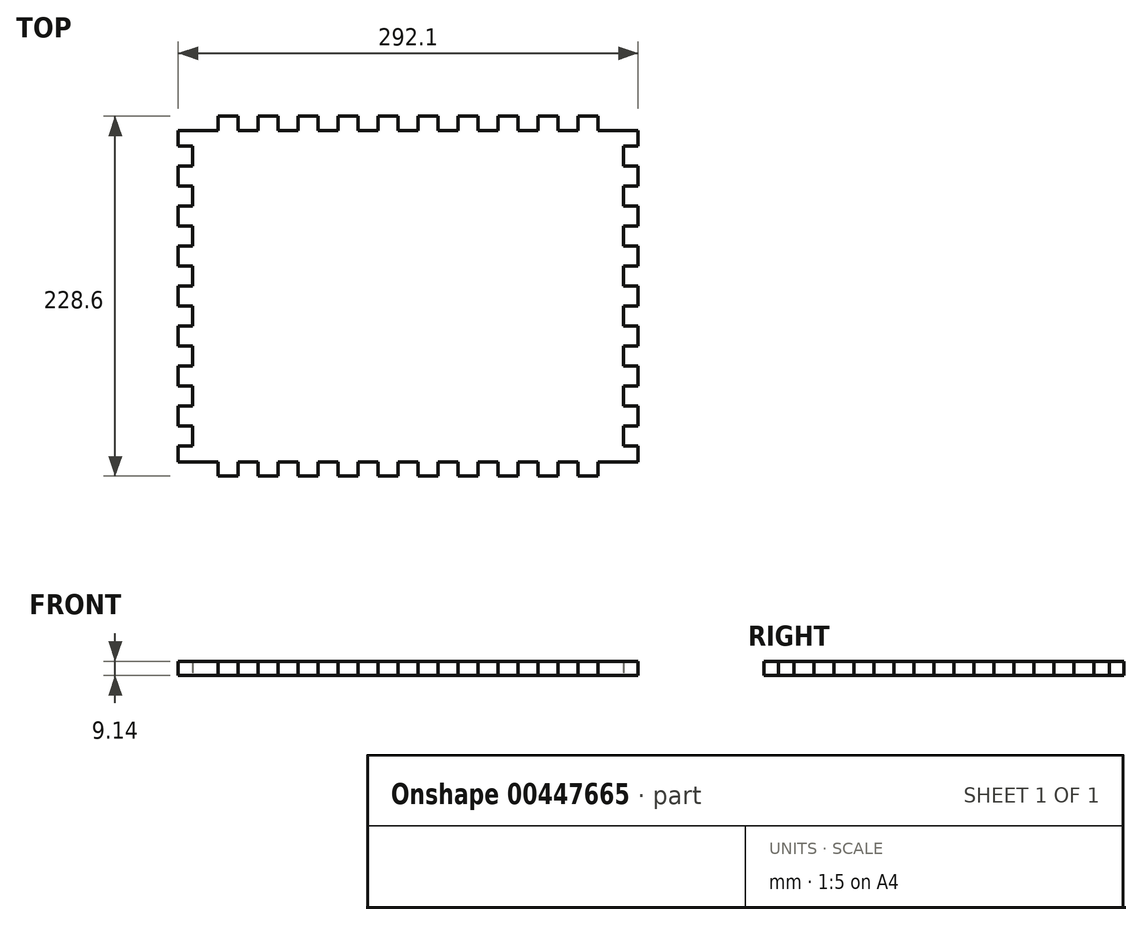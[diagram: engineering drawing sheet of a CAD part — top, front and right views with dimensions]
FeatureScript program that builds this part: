
annotation { "Feature Type Name" : "Feature", "Feature Type Description" : "" }
export const myFeature = defineFeature(function(context is Context, id is Id, definition is map)
    precondition{}
    {
        {
            var Q0;
            Q0=qCreatedBy(makeId("Top.planeOp"),FACE);
            var sketch = newSketch(context, id + "F0", { "sketchPlane" : qUnion([Q0])});
            skLineSegment(sketch, "E0.left", {"start": v(0, -9.14) * mm, "end": v(0, -19.05) * mm});
            skPoint(sketch, "E1.orphan", {"position": v(0, 0) * mm});
            skLineSegment(sketch, "E2", {"start": v(0, -9.14) * mm, "end": v(25.4, -9.14) * mm});
            skLineSegment(sketch, "E3", {"start": v(25.4, -9.14) * mm, "end": v(25.4, 0) * mm});
            skLineSegment(sketch, "E4", {"start": v(25.4, 0) * mm, "end": v(38.1, 0) * mm});
            skLineSegment(sketch, "E5", {"start": v(38.1, 0) * mm, "end": v(38.1, -9.14) * mm});
            skLineSegment(sketch, "E6", {"start": v(38.1, -9.14) * mm, "end": v(50.8, -9.14) * mm});
            skLineSegment(sketch, "E7", {"start": v(50.8, -9.14) * mm, "end": v(50.8, 0) * mm});
            skLineSegment(sketch, "E8", {"start": v(50.8, 0) * mm, "end": v(63.5, 0) * mm});
            skLineSegment(sketch, "E9", {"start": v(63.5, 0) * mm, "end": v(63.5, -9.14) * mm});
            skLineSegment(sketch, "E10", {"start": v(63.5, -9.14) * mm, "end": v(76.2, -9.14) * mm});
            skLineSegment(sketch, "E11", {"start": v(76.2, -9.14) * mm, "end": v(76.2, 0) * mm});
            skLineSegment(sketch, "E12.trimOffspring", {"start": v(76.2, 0) * mm, "end": v(88.9, 0) * mm});
            skLineSegment(sketch, "E13", {"start": v(88.9, 0) * mm, "end": v(88.9, -9.14) * mm});
            skLineSegment(sketch, "E14", {"start": v(88.9, -9.14) * mm, "end": v(101.6, -9.14) * mm});
            skLineSegment(sketch, "E15", {"start": v(101.6, -9.14) * mm, "end": v(101.6, 0) * mm});
            skLineSegment(sketch, "E16", {"start": v(101.6, 0) * mm, "end": v(114.3, 0) * mm});
            skLineSegment(sketch, "E17", {"start": v(114.3, 0) * mm, "end": v(114.3, -9.14) * mm});
            skLineSegment(sketch, "E18", {"start": v(114.3, -9.14) * mm, "end": v(127, -9.14) * mm});
            skLineSegment(sketch, "E19", {"start": v(127, -9.14) * mm, "end": v(127, 0) * mm});
            skLineSegment(sketch, "E20.trimOffspring", {"start": v(127, 0) * mm, "end": v(139.7, 0) * mm});
            skLineSegment(sketch, "E21", {"start": v(139.7, 0) * mm, "end": v(139.7, -9.14) * mm});
            skLineSegment(sketch, "E22", {"start": v(139.7, -9.14) * mm, "end": v(152.4, -9.14) * mm});
            skLineSegment(sketch, "E23", {"start": v(152.4, -9.14) * mm, "end": v(152.4, 0) * mm});
            skLineSegment(sketch, "E24", {"start": v(152.4, 0) * mm, "end": v(165.1, 0) * mm});
            skLineSegment(sketch, "E25", {"start": v(165.1, 0) * mm, "end": v(165.1, -9.14) * mm});
            skLineSegment(sketch, "E26", {"start": v(165.1, -9.14) * mm, "end": v(177.8, -9.14) * mm});
            skLineSegment(sketch, "E27", {"start": v(177.8, -9.14) * mm, "end": v(177.8, 0) * mm});
            skLineSegment(sketch, "E28.trimOffspring", {"start": v(177.8, 0) * mm, "end": v(190.5, 0) * mm});
            skLineSegment(sketch, "E29", {"start": v(190.5, 0) * mm, "end": v(190.5, -9.14) * mm});
            skLineSegment(sketch, "E30", {"start": v(190.5, -9.14) * mm, "end": v(203.2, -9.14) * mm});
            skLineSegment(sketch, "E31", {"start": v(203.2, -9.14) * mm, "end": v(203.2, 0) * mm});
            skLineSegment(sketch, "E32", {"start": v(203.2, 0) * mm, "end": v(215.9, 0) * mm});
            skLineSegment(sketch, "E33", {"start": v(215.9, 0) * mm, "end": v(215.9, -9.14) * mm});
            skLineSegment(sketch, "E34", {"start": v(215.9, -9.14) * mm, "end": v(228.6, -9.14) * mm});
            skLineSegment(sketch, "E35", {"start": v(228.6, -9.14) * mm, "end": v(228.6, 0) * mm});
            skLineSegment(sketch, "E36.trimOffspring", {"start": v(228.6, 0) * mm, "end": v(241.3, 0) * mm});
            skLineSegment(sketch, "E37", {"start": v(241.3, 0) * mm, "end": v(241.3, -9.14) * mm});
            skLineSegment(sketch, "E38", {"start": v(241.3, -9.14) * mm, "end": v(254, -9.14) * mm});
            skLineSegment(sketch, "E39", {"start": v(254, -9.14) * mm, "end": v(254, 0) * mm});
            skLineSegment(sketch, "E40", {"start": v(254, 0) * mm, "end": v(266.7, 0) * mm});
            skLineSegment(sketch, "E41", {"start": v(266.7, 0) * mm, "end": v(266.7, -9.14) * mm});
            skLineSegment(sketch, "E42", {"start": v(266.7, -9.14) * mm, "end": v(292.1, -9.14) * mm});
            skPoint(sketch, "E43.orphan", {"position": v(292.1, 0) * mm});
            skPoint(sketch, "E44.orphan", {"position": v(0, -228.6) * mm});
            skLineSegment(sketch, "E45", {"start": v(0.16, -114.3) * mm, "end": v(38.79, -114.3) * mm, "construction": true});
            skLineSegment(sketch, "E46.MirrorCS", {"start": v(101.6, -228.6) * mm, "end": v(114.3, -228.6) * mm});
            skLineSegment(sketch, "E47.MirrorCS", {"start": v(114.3, -228.6) * mm, "end": v(114.3, -219.46) * mm});
            skLineSegment(sketch, "E48.MirrorCS", {"start": v(114.3, -219.46) * mm, "end": v(127, -219.46) * mm});
            skLineSegment(sketch, "E49.MirrorCS", {"start": v(127, -219.46) * mm, "end": v(127, -228.6) * mm});
            skLineSegment(sketch, "E50.MirrorCS", {"start": v(127, -228.6) * mm, "end": v(139.7, -228.6) * mm});
            skLineSegment(sketch, "E51.MirrorCS", {"start": v(139.7, -228.6) * mm, "end": v(139.7, -219.46) * mm});
            skLineSegment(sketch, "E52.MirrorCS", {"start": v(139.7, -219.46) * mm, "end": v(152.4, -219.46) * mm});
            skLineSegment(sketch, "E53.MirrorCS", {"start": v(152.4, -219.46) * mm, "end": v(152.4, -228.6) * mm});
            skLineSegment(sketch, "E54.MirrorCS", {"start": v(152.4, -228.6) * mm, "end": v(165.1, -228.6) * mm});
            skLineSegment(sketch, "E55.MirrorCS", {"start": v(165.1, -228.6) * mm, "end": v(165.1, -219.46) * mm});
            skLineSegment(sketch, "E56.MirrorCS", {"start": v(165.1, -219.46) * mm, "end": v(177.8, -219.46) * mm});
            skLineSegment(sketch, "E57.MirrorCS", {"start": v(177.8, -219.46) * mm, "end": v(177.8, -228.6) * mm});
            skLineSegment(sketch, "E58.MirrorCS", {"start": v(177.8, -228.6) * mm, "end": v(190.5, -228.6) * mm});
            skLineSegment(sketch, "E59.MirrorCS", {"start": v(190.5, -228.6) * mm, "end": v(190.5, -219.46) * mm});
            skLineSegment(sketch, "E60.MirrorCS", {"start": v(190.5, -219.46) * mm, "end": v(203.2, -219.46) * mm});
            skLineSegment(sketch, "E61.MirrorCS", {"start": v(203.2, -219.46) * mm, "end": v(203.2, -228.6) * mm});
            skLineSegment(sketch, "E62.MirrorCS", {"start": v(203.2, -228.6) * mm, "end": v(215.9, -228.6) * mm});
            skLineSegment(sketch, "E63.MirrorCS", {"start": v(215.9, -228.6) * mm, "end": v(215.9, -219.46) * mm});
            skLineSegment(sketch, "E64.MirrorCS", {"start": v(215.9, -219.46) * mm, "end": v(228.6, -219.46) * mm});
            skLineSegment(sketch, "E65.MirrorCS", {"start": v(228.6, -219.46) * mm, "end": v(228.6, -228.6) * mm});
            skLineSegment(sketch, "E66.MirrorCS", {"start": v(228.6, -228.6) * mm, "end": v(241.3, -228.6) * mm});
            skLineSegment(sketch, "E67.MirrorCS", {"start": v(241.3, -228.6) * mm, "end": v(241.3, -219.46) * mm});
            skLineSegment(sketch, "E68.MirrorCS", {"start": v(254, -228.6) * mm, "end": v(266.7, -228.6) * mm});
            skLineSegment(sketch, "E69.MirrorCS", {"start": v(254, -219.46) * mm, "end": v(254, -228.6) * mm});
            skLineSegment(sketch, "E70.MirrorCS", {"start": v(241.3, -219.46) * mm, "end": v(254, -219.46) * mm});
            skLineSegment(sketch, "E71.MirrorCS", {"start": v(266.7, -228.6) * mm, "end": v(266.7, -219.46) * mm});
            skLineSegment(sketch, "E72.MirrorCS", {"start": v(266.7, -219.46) * mm, "end": v(292.1, -219.46) * mm});
            skLineSegment(sketch, "E73", {"start": v(0, -19.05) * mm, "end": v(9.14, -19.05) * mm});
            skLineSegment(sketch, "E74", {"start": v(9.14, -19.05) * mm, "end": v(9.14, -31.75) * mm});
            skLineSegment(sketch, "E75", {"start": v(9.14, -31.75) * mm, "end": v(0, -31.75) * mm});
            skLineSegment(sketch, "E76", {"start": v(0, -31.75) * mm, "end": v(0, -44.45) * mm});
            skLineSegment(sketch, "E77", {"start": v(0, -44.45) * mm, "end": v(9.14, -44.45) * mm});
            skLineSegment(sketch, "E78", {"start": v(9.14, -44.45) * mm, "end": v(9.14, -57.15) * mm});
            skLineSegment(sketch, "E79", {"start": v(9.14, -57.15) * mm, "end": v(0, -57.15) * mm});
            skLineSegment(sketch, "E80.trimOffspring", {"start": v(0, -57.15) * mm, "end": v(0, -69.85) * mm});
            skLineSegment(sketch, "E81", {"start": v(0, -69.85) * mm, "end": v(9.14, -69.85) * mm});
            skLineSegment(sketch, "E82", {"start": v(9.14, -69.85) * mm, "end": v(9.14, -82.55) * mm});
            skLineSegment(sketch, "E83", {"start": v(9.14, -82.55) * mm, "end": v(0, -82.55) * mm});
            skLineSegment(sketch, "E84", {"start": v(0, -82.55) * mm, "end": v(0, -95.25) * mm});
            skLineSegment(sketch, "E85", {"start": v(0, -95.25) * mm, "end": v(9.14, -95.25) * mm});
            skLineSegment(sketch, "E86", {"start": v(9.14, -95.25) * mm, "end": v(9.14, -107.95) * mm});
            skLineSegment(sketch, "E87", {"start": v(9.14, -107.95) * mm, "end": v(0, -107.95) * mm});
            skLineSegment(sketch, "E88.trimOffspring", {"start": v(0, -107.95) * mm, "end": v(0, -120.65) * mm});
            skLineSegment(sketch, "E89", {"start": v(0, -120.65) * mm, "end": v(9.14, -120.65) * mm});
            skLineSegment(sketch, "E90", {"start": v(9.14, -120.65) * mm, "end": v(9.14, -133.35) * mm});
            skLineSegment(sketch, "E91", {"start": v(9.14, -133.35) * mm, "end": v(0, -133.35) * mm});
            skLineSegment(sketch, "E92", {"start": v(0, -133.35) * mm, "end": v(0, -146.05) * mm});
            skLineSegment(sketch, "E93", {"start": v(0, -146.05) * mm, "end": v(9.14, -146.05) * mm});
            skLineSegment(sketch, "E94", {"start": v(9.14, -146.05) * mm, "end": v(9.14, -158.75) * mm});
            skLineSegment(sketch, "E95", {"start": v(9.14, -158.75) * mm, "end": v(0, -158.75) * mm});
            skLineSegment(sketch, "E96.trimOffspring", {"start": v(0, -158.75) * mm, "end": v(0, -171.45) * mm});
            skLineSegment(sketch, "E97", {"start": v(146.05, -9.14) * mm, "end": v(146.05, -55.68) * mm, "construction": true});
            skPoint(sketch, "E97.endSnap0", {"position": v(146.05, -9.14) * mm});
            skLineSegment(sketch, "E98.MirrorCS", {"start": v(292.1, -9.14) * mm, "end": v(292.1, -19.05) * mm});
            skLineSegment(sketch, "E99.MirrorCS", {"start": v(292.1, -19.05) * mm, "end": v(282.96, -19.05) * mm});
            skLineSegment(sketch, "E100.MirrorCS", {"start": v(282.96, -19.05) * mm, "end": v(282.96, -31.75) * mm});
            skLineSegment(sketch, "E101.MirrorCS", {"start": v(282.96, -31.75) * mm, "end": v(292.1, -31.75) * mm});
            skLineSegment(sketch, "E102.MirrorCS", {"start": v(292.1, -31.75) * mm, "end": v(292.1, -44.45) * mm});
            skLineSegment(sketch, "E103.MirrorCS", {"start": v(292.1, -44.45) * mm, "end": v(282.96, -44.45) * mm});
            skLineSegment(sketch, "E104.MirrorCS", {"start": v(282.96, -44.45) * mm, "end": v(282.96, -57.15) * mm});
            skLineSegment(sketch, "E105.MirrorCS", {"start": v(282.96, -57.15) * mm, "end": v(292.1, -57.15) * mm});
            skLineSegment(sketch, "E106.MirrorCS", {"start": v(292.1, -57.15) * mm, "end": v(292.1, -69.85) * mm});
            skLineSegment(sketch, "E107.MirrorCS", {"start": v(292.1, -69.85) * mm, "end": v(282.96, -69.85) * mm});
            skLineSegment(sketch, "E108.MirrorCS", {"start": v(282.96, -69.85) * mm, "end": v(282.96, -82.55) * mm});
            skLineSegment(sketch, "E109.MirrorCS", {"start": v(282.96, -82.55) * mm, "end": v(292.1, -82.55) * mm});
            skLineSegment(sketch, "E110.MirrorCS", {"start": v(292.1, -82.55) * mm, "end": v(292.1, -95.25) * mm});
            skLineSegment(sketch, "E111.MirrorCS", {"start": v(292.1, -95.25) * mm, "end": v(282.96, -95.25) * mm});
            skLineSegment(sketch, "E112.MirrorCS", {"start": v(282.96, -95.25) * mm, "end": v(282.96, -107.95) * mm});
            skLineSegment(sketch, "E113.MirrorCS", {"start": v(282.96, -107.95) * mm, "end": v(292.1, -107.95) * mm});
            skLineSegment(sketch, "E114.MirrorCS", {"start": v(292.1, -107.95) * mm, "end": v(292.1, -120.65) * mm});
            skLineSegment(sketch, "E115.MirrorCS", {"start": v(292.1, -120.65) * mm, "end": v(282.96, -120.65) * mm});
            skLineSegment(sketch, "E116.MirrorCS", {"start": v(282.96, -120.65) * mm, "end": v(282.96, -133.35) * mm});
            skLineSegment(sketch, "E117.MirrorCS", {"start": v(282.96, -133.35) * mm, "end": v(292.1, -133.35) * mm});
            skLineSegment(sketch, "E118.MirrorCS", {"start": v(292.1, -133.35) * mm, "end": v(292.1, -146.05) * mm});
            skLineSegment(sketch, "E119.MirrorCS", {"start": v(292.1, -146.05) * mm, "end": v(282.96, -146.05) * mm});
            skLineSegment(sketch, "E120.MirrorCS", {"start": v(282.96, -146.05) * mm, "end": v(282.96, -158.75) * mm});
            skLineSegment(sketch, "E121.MirrorCS", {"start": v(282.96, -158.75) * mm, "end": v(292.1, -158.75) * mm});
            skLineSegment(sketch, "E122", {"start": v(0, -171.45) * mm, "end": v(9.14, -171.45) * mm});
            skLineSegment(sketch, "E123", {"start": v(9.14, -171.45) * mm, "end": v(9.14, -184.15) * mm});
            skLineSegment(sketch, "E124", {"start": v(9.14, -184.15) * mm, "end": v(0, -184.15) * mm});
            skLineSegment(sketch, "E125.MirrorCS", {"start": v(0, -219.46) * mm, "end": v(0, -209.55) * mm});
            skLineSegment(sketch, "E126.MirrorCS", {"start": v(0, -209.55) * mm, "end": v(9.14, -209.55) * mm});
            skLineSegment(sketch, "E127.MirrorCS", {"start": v(9.14, -209.55) * mm, "end": v(9.14, -196.85) * mm});
            skLineSegment(sketch, "E128.MirrorCS", {"start": v(9.14, -196.85) * mm, "end": v(0, -196.85) * mm});
            skLineSegment(sketch, "E129.MirrorCS", {"start": v(0, -196.85) * mm, "end": v(0, -184.15) * mm});
            skLineSegment(sketch, "E130.MirrorCS", {"start": v(292.1, -219.46) * mm, "end": v(292.1, -209.55) * mm});
            skLineSegment(sketch, "E131.MirrorCS", {"start": v(292.1, -209.55) * mm, "end": v(282.96, -209.55) * mm});
            skLineSegment(sketch, "E132.MirrorCS", {"start": v(282.96, -209.55) * mm, "end": v(282.96, -196.85) * mm});
            skLineSegment(sketch, "E133.MirrorCS", {"start": v(282.96, -196.85) * mm, "end": v(292.1, -196.85) * mm});
            skLineSegment(sketch, "E134.MirrorCS", {"start": v(292.1, -196.85) * mm, "end": v(292.1, -184.15) * mm});
            skLineSegment(sketch, "E135.MirrorCS", {"start": v(282.96, -184.15) * mm, "end": v(292.1, -184.15) * mm});
            skLineSegment(sketch, "E136.MirrorCS", {"start": v(282.96, -171.45) * mm, "end": v(282.96, -184.15) * mm});
            skLineSegment(sketch, "E137.MirrorCS", {"start": v(292.1, -171.45) * mm, "end": v(282.96, -171.45) * mm});
            skLineSegment(sketch, "E138.MirrorCS", {"start": v(292.1, -158.75) * mm, "end": v(292.1, -171.45) * mm});
            skLineSegment(sketch, "E139.MirrorCS", {"start": v(0, -219.46) * mm, "end": v(25.4, -219.46) * mm});
            skLineSegment(sketch, "E140.MirrorCS", {"start": v(25.4, -219.46) * mm, "end": v(25.4, -228.6) * mm});
            skLineSegment(sketch, "E141.MirrorCS", {"start": v(25.4, -228.6) * mm, "end": v(38.1, -228.6) * mm});
            skLineSegment(sketch, "E142.MirrorCS", {"start": v(38.1, -228.6) * mm, "end": v(38.1, -219.46) * mm});
            skLineSegment(sketch, "E143.MirrorCS", {"start": v(38.1, -219.46) * mm, "end": v(50.8, -219.46) * mm});
            skLineSegment(sketch, "E144.MirrorCS", {"start": v(50.8, -219.46) * mm, "end": v(50.8, -228.6) * mm});
            skLineSegment(sketch, "E145.MirrorCS", {"start": v(50.8, -228.6) * mm, "end": v(63.5, -228.6) * mm});
            skLineSegment(sketch, "E146.MirrorCS", {"start": v(63.5, -228.6) * mm, "end": v(63.5, -219.46) * mm});
            skLineSegment(sketch, "E147.MirrorCS", {"start": v(63.5, -219.46) * mm, "end": v(76.2, -219.46) * mm});
            skLineSegment(sketch, "E148.MirrorCS", {"start": v(76.2, -219.46) * mm, "end": v(76.2, -228.6) * mm});
            skLineSegment(sketch, "E149.MirrorCS", {"start": v(76.2, -228.6) * mm, "end": v(88.9, -228.6) * mm});
            skLineSegment(sketch, "E150.MirrorCS", {"start": v(88.9, -228.6) * mm, "end": v(88.9, -219.46) * mm});
            skLineSegment(sketch, "E151.MirrorCS", {"start": v(88.9, -219.46) * mm, "end": v(101.6, -219.46) * mm});
            skLineSegment(sketch, "E152.MirrorCS", {"start": v(101.6, -219.46) * mm, "end": v(101.6, -228.6) * mm});
            skSolve(sketch);
        }
        {
            var Q0;
            Q0 = qSketchRegion(id + "F0", true);
            extrude(context, id + "F1", {"entities" : qUnion([Q0]), "depth" : 9.14 * mm});
        }
    });
